# Revit family: Sirius_Three_FS_50,70kW_LOD-5
name_source: partatom
category: Mechanical Equipment
revit_build: Autodesk Revit 2017 (Build: 20160225_1515(x64)
units: mm (PartAtom-declared; Revit-internal decimal feet)

## family parameters
Always vertical = Yes
Cut with Voids When Loaded = No
OmniClass Number = 23.75.10.11.14.14
OmniClass Title = Condensing Boilers
Part Type = Normal
Room Calculation Point = No
Round Connector Dimension = Use Diameter
Shared = No
Work Plane-Based = No

## types (2) — shared parameters
6 Monthly = 0
Access Clearance Bottom = 0 mm
Access Clearance Front = 1000 mm
Access Clearance Left = 500 mm
Access Clearance Rear = 320 mm
Access Clearance Right = 500 mm
Access Clearance Top = 250 mm
Additional Technical Details = Cascade kits available for up to 6 boilers
Air Inlet Connection Size = 125 mm
Annually = Annual service according to manufacturers guidance.
BMS Links = Yes
Bespoke Timeframe = 0
Burner Control Type = Modulating
CE Mark = CE-0085CP0089
Colour = White
Condensate Drain Size = 18 mm
Condensate Drain Type = Plain
Configuration = Single boiler
Control Type = Optimised, modulating, weather compensating, BMS compatible
Daily = 0
Drain Connection Size = 0 mm
Drain Connection Type = Plain
Embodied Carbon = 0
Environmental Product Declaration = 0
ErP Energy Label = A
ErP Seasonal Efficiency = 93 %
External Material = Steel
Features = Floor standing boiler, stainless steel heat exchanger, 9:1 modulation
Finish = Powder coated
Flow and Return Connection Size = 25 mm
Flow and Return Connection Type = Threaded
Flue Connection size = 80 mm
Flue or Air Intake Classification = C13; C33; B23; B23p; C43; C53; C63; C83
Frequency = 50 Hz
Fuel Connection Size = 19 mm
Fuel Connection Type = Threaded
Fuse Rating = 3 A
Gas Consumption rate = Various
Green Guide for Specification = 0
Heat Exchanger Material = Stainless Steel
Heater Operation = Condensing
Hydraulic Resistance at 11C temperature differential = 0.000
IK Rating = 0
IP Rating = IP21
IfcExportAs = IfcBoilerType
IfcExportType = NOTDEFINED
Interlocks = Yes
Life Cycle Analysis = 0
Location of Manufacturer = 0
Maintenance Required 0 to 300hrs = 0
Maintenance Required 1001 to 2000hrs = 0
Maintenance Required 2001 to 4000hrs = 0
Maintenance Required 301 to 600hrs = 0
Maintenance Required 4001 to 8000hrs = 0
Maintenance Required 601 to 1000hrs = 0
Maintenance Required 8001 to 12000hrs = 0
Manufacturer = Potterton Commercial
Manufacturer Website = http://www.pottertoncommercial.co.uk
Material Ingredient Reporting = 0
Maximum Gas Inlet Pressure = 25.000 bar
Maximum Oil Inlet Pressure = 0.000 bar
Maximum Operating Pressure = 4.000 bar
Minimum Flow Rate at 11C temperature differential = 0.000 L/s
Minimum Gas Inlet Pressure = 0.017 bar
Minimum Oil Inlet Pressure = 0.000 bar
Minimum Operating Pressure = 1.000 bar
Minimum Power Consumption = 3 W
Model = SIRIUS two FS50
Monthly = 0
Mounting = Floor Standing
Nominal Gas Inlet Pressure = 0.020 bar
Nominal Oil Inlet Pressure = 0.000 bar
Optional Fuel = Gas - LPG
Overall Height = 848 mm
Overall Length = 681 mm
Overall Width = 600 mm
Primary Fuel = Gas - NG
Product Literature = ww.pottertoncommercial.co.uk/products/stainless-steel/sirius-two-fs-50-110kW.htm
Product Model Number = 5142181
Product Range = Sirius two FS (70kW)
Quarterly = 0
Rated Criteria = 80/60
Reference Standard = ISO 9001; ISO 14001
Responsible Extraction of Materials = 0
Responsible Sourcing of Materials = 0
Safety Valve Connection Size = 0 mm
Safety Valve Connection Type = Threaded
Shape = Rectangular (Vertical)
Starting Current = 0 A
Supply Phase = 1
Turndown Ratio = 9:1
Uniclass2015 = Pr_60_60_08_34
Voltage = 230 V
Warranty ID = See manufacturers website for warranty options and T&C's
Water Treatment Required = Yes
Weekly = 0
zero-valued in all types: Oil Consumption rate

## per-type parameters (varying)
| type | Building Regulations Seasonal Efficiency | ErP Rated Efficiency at Full Load | ErP Rated Efficiency at Part Load | Full Load Current | Gross Weight | Hydraulic Resistance at 15C temperature differential | Hydraulic Resistance at 20C temperature differential | Maximum Power Consumption | Minimum Flow Rate at 15C temperature differential | Minimum Flow Rate at 20C temperature differential | NOx Emissions | Operation and Maintenance Manual | Rated Output | Shipping Weight | Sound Pressure Level | Water Content |
| 70kW FS | 96.9 % | 87.6 % | 97.4 % | 1 A | 70.00 kg | 0.520 | 0.320 | 117 W | 1.040 L/s | 0.780 L/s | 31 mg/kWh | http://www.pottertoncommercial.co.uk | 65000 W | 70.00 kg | 64 dBA | 5.0 L |
| 50kW FS | 97.1 % | 87.7 % | 97.7 % | 0 A | 60.00 kg | 0.940 | 0.540 | 100 W | 0.720 L/s | 0.540 L/s | 27 mg/kWh | https://www.pottertoncommercial.co.uk | 45000 W | 60.00 kg | 61 dB | 2.8 L |

note: source unit labels omitted for Hydraulic Resistance at 11C temperature differential, Hydraulic Resistance at 15C temperature differential, Hydraulic Resistance at 20C temperature differential — the stored unit's dimension contradicts the parameter name (converter mislabeling)

## geometry (parser evidence)
native form markers: Blend x2, Sweep x8
no freeform markers — native parametric forms only
